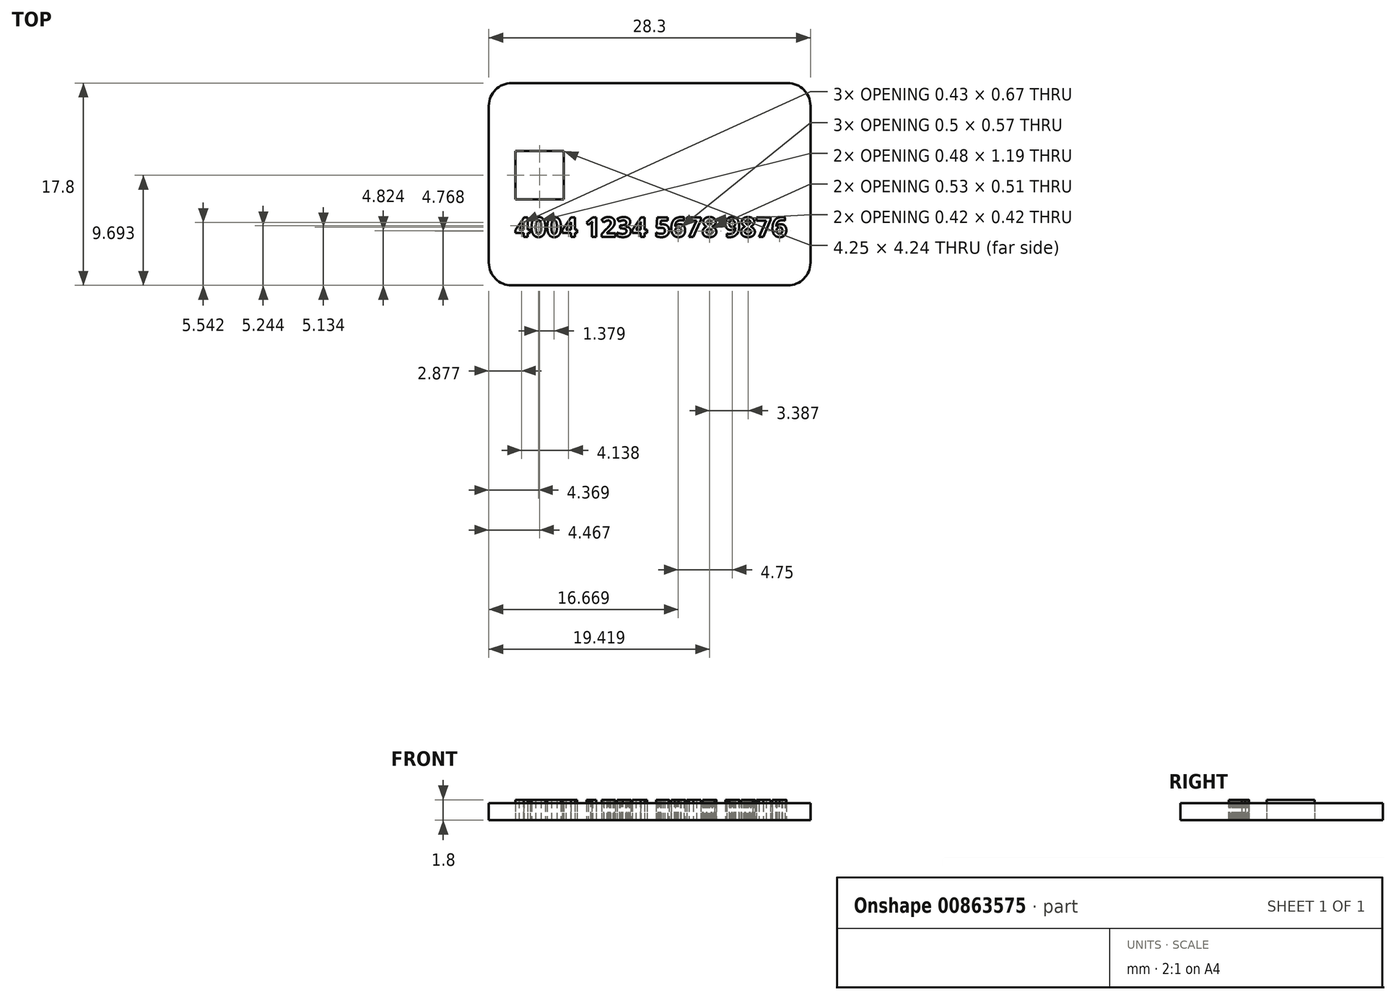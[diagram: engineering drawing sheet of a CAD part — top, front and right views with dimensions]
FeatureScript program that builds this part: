
annotation { "Feature Type Name" : "Feature", "Feature Type Description" : "" }
export const myFeature = defineFeature(function(context is Context, id is Id, definition is map)
    precondition{}
    {
        {
            var Q0;
            Q0=qCreatedBy(makeId("Top.planeOp"),FACE);
            var sketch = newSketch(context, id + "F0", { "sketchPlane" : qUnion([Q0])});
            skLineSegment(sketch, "E0.bottom", {"start": v(-21.54, 8.61) * mm, "end": v(2.76, 8.61) * mm});
            skLineSegment(sketch, "E0.top", {"start": v(-21.54, -9.19) * mm, "end": v(2.76, -9.19) * mm});
            skLineSegment(sketch, "E0.left", {"start": v(-23.54, 6.61) * mm, "end": v(-23.54, -7.19) * mm});
            skLineSegment(sketch, "E0.right", {"start": v(4.76, 6.61) * mm, "end": v(4.76, -7.19) * mm});
            skPoint(sketch, "E1.visualSharp", {"position": v(-23.54, 8.61) * mm});
            skArc(sketch, "E1.filletArc", {"start": v(-21.54, 8.61) * mm, "mid": v(-22.95, 8.03) * mm, "end": v(-23.54, 6.61) * mm});
            skPoint(sketch, "E2.visualSharp", {"position": v(4.76, 8.61) * mm});
            skArc(sketch, "E2.filletArc", {"start": v(4.76, 6.61) * mm, "mid": v(4.18, 8.03) * mm, "end": v(2.76, 8.61) * mm});
            skPoint(sketch, "E3.visualSharp", {"position": v(-23.54, -9.19) * mm});
            skArc(sketch, "E3.filletArc", {"start": v(-23.54, -7.19) * mm, "mid": v(-22.95, -8.6) * mm, "end": v(-21.54, -9.19) * mm});
            skPoint(sketch, "E4.visualSharp", {"position": v(4.76, -9.19) * mm});
            skArc(sketch, "E4.filletArc", {"start": v(2.76, -9.19) * mm, "mid": v(4.18, -8.6) * mm, "end": v(4.76, -7.19) * mm});
            skLineSegment(sketch, "E5.bottom", {"start": v(-21.2, 2.62) * mm, "end": v(-16.95, 2.62) * mm});
            skLineSegment(sketch, "E5.top", {"start": v(-21.2, -1.61) * mm, "end": v(-16.95, -1.61) * mm});
            skLineSegment(sketch, "E5.left", {"start": v(-21.2, 2.62) * mm, "end": v(-21.2, -1.61) * mm});
            skLineSegment(sketch, "E5.right", {"start": v(-16.95, 2.62) * mm, "end": v(-16.95, -1.61) * mm});
            skLineSegment(sketch, "E6.bottom", {"start": v(-19.7, 1.1) * mm, "end": v(-18.4, 1.1) * mm});
            skLineSegment(sketch, "E6.top", {"start": v(-19.7, -0.28) * mm, "end": v(-18.4, -0.28) * mm});
            skLineSegment(sketch, "E6.left", {"start": v(-19.7, 1.1) * mm, "end": v(-19.7, -0.28) * mm});
            skLineSegment(sketch, "E6.right", {"start": v(-18.4, 1.1) * mm, "end": v(-18.4, -0.28) * mm});
            skSolve(sketch);
        }
        {
            var Q0;
            Q0=qCreatedBy(makeId("Top.planeOp"),FACE);
            var sketch = newSketch(context, id + "F1", { "sketchPlane" : qUnion([Q0])});
            skText(sketch, "E7", { "text": "4004 1234 5678 9876", "fontName": "OpenSans-Bold.ttf"});
            const initialGuessF1  = {"E7": [-0.02124, -0.00492, 1, 0, 0.00174]};
            skSetInitialGuess(sketch, initialGuessF1);
            skSolve(sketch);
        }
        {
            var Q0;
            Q0 = qSketchRegion(id + "F1", true);
            extrude(context, id + "F2", {"entities" : qUnion([Q0]), "depth" : 1.8 * mm, "offsetDistance" : 25 * mm});
        }
        {
            var Q0;
            Q0=makeQuery(id+"F0.imprint","IMPRINT",FACE,{"disambiguationData":[TD([[makeQuery(id+"F0.imprint","IMPRINT",EDGE,{"derivedFrom":sQuery(id+"F0.wireOp",EDGE,"E6.bottom")}),-1.0]])]});
            var Q1;
            Q1=makeQuery(id+"F0.imprint","IMPRINT",FACE,{"disambiguationData":[TD([[makeQuery(id+"F0.imprint","IMPRINT",EDGE,{"derivedFrom":sQuery(id+"F0.wireOp",EDGE,"E5.bottom")}),-1.0]])]});
            extrude(context, id + "F3", {"entities" : qUnion([Q0, Q1]), "depth" : 1.8 * mm, "offsetDistance" : 25 * mm});
        }
        {
            var Q0;
            Q0=makeQuery(id+"F0.imprint","IMPRINT",FACE,{"disambiguationData":[TD([[makeQuery(id+"F0.imprint","IMPRINT",EDGE,{"derivedFrom":sQuery(id+"F0.wireOp",EDGE,"E0.bottom")}),-1.0]])]});
            extrude(context, id + "F4", {"entities" : qUnion([Q0]), "depth" : 1.5 * mm, "offsetDistance" : 25 * mm});
        }
    });
